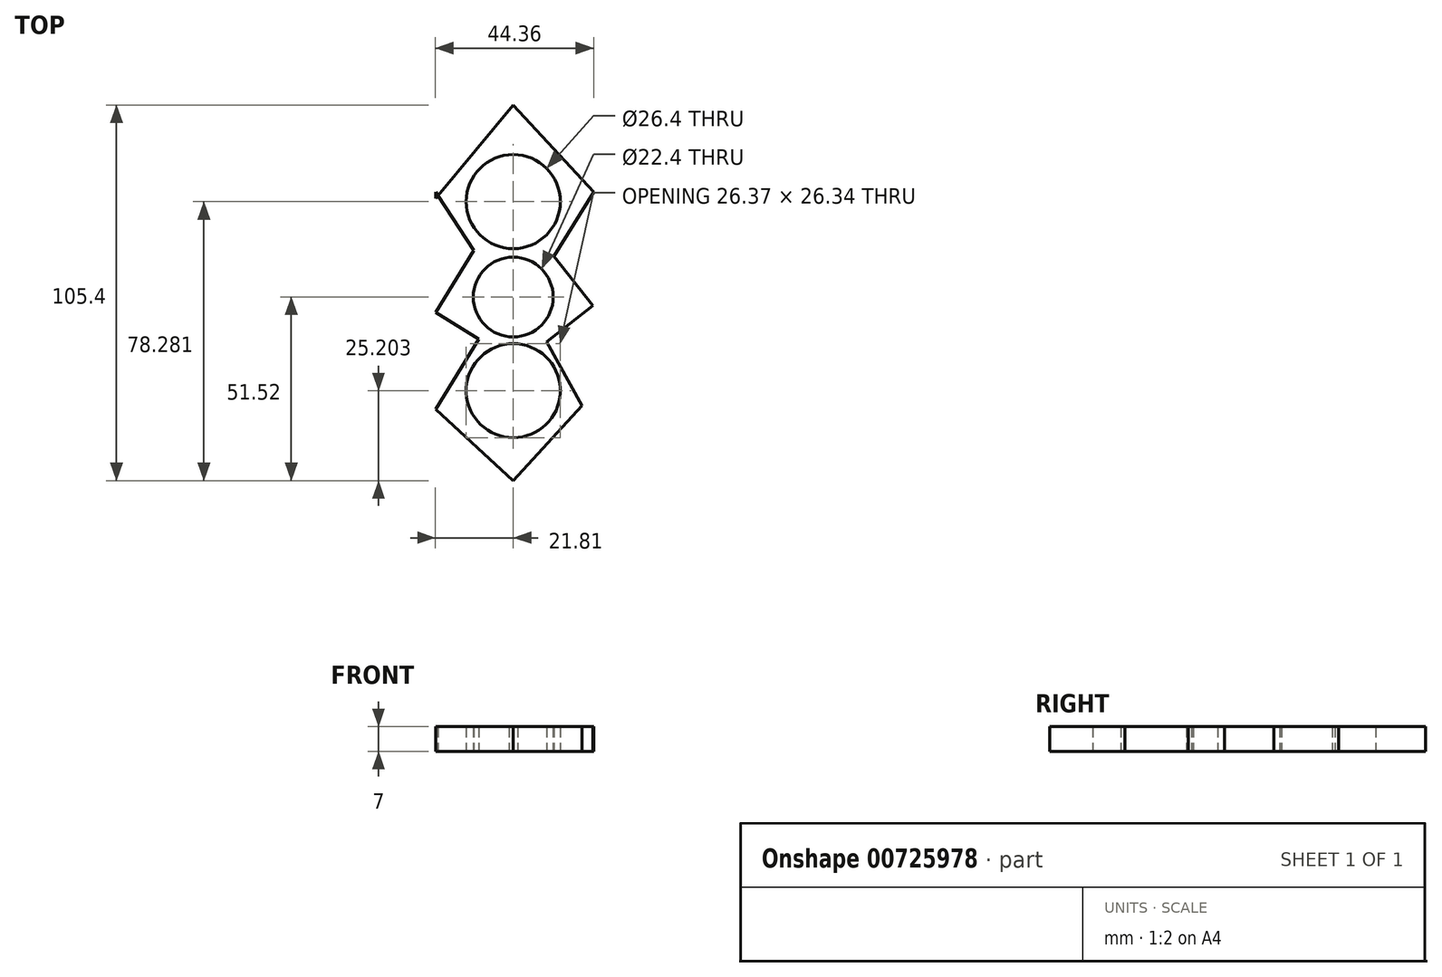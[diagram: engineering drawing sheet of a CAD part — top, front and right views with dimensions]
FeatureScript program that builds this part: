
annotation { "Feature Type Name" : "Feature", "Feature Type Description" : "" }
export const myFeature = defineFeature(function(context is Context, id is Id, definition is map)
    precondition{}
    {
        {
            var Q0;
            Q0=qCreatedBy(makeId("Top.planeOp"),FACE);
            var sketch = newSketch(context, id + "F0", { "sketchPlane" : qUnion([Q0])});
            skCircle(sketch, "E0", {"center": v(0, 26.76) * mm, "radius": 13.2 * mm});
            skCircle(sketch, "E1", {"center": v(0, 26.76) * mm, "radius": 11.2 * mm});
            skCircle(sketch, "E2", {"center": v(0, 0) * mm, "radius": 11.2 * mm});
            skArc(sketch, "E3", {"start": v(-1.2, -13.14) * mm, "mid": v(0, -39.49) * mm, "end": v(1.2, -13.14) * mm});
            skCircle(sketch, "E4", {"center": v(0, -26.29) * mm, "radius": 11.2 * mm});
            skLineSegment(sketch, "E5", {"start": v(-1.2, -13.14) * mm, "end": v(1.2, -13.14) * mm});
            skLineSegment(sketch, "E6", {"start": v(-21.8, 29.5) * mm, "end": v(-21.8, 27.7) * mm});
            skLineSegment(sketch, "E7", {"start": v(-21.8, 29.5) * mm, "end": v(-11.1, 13.07) * mm});
            skLineSegment(sketch, "E8", {"start": v(-11.1, 13.07) * mm, "end": v(-21.8, -4.36) * mm});
            skLineSegment(sketch, "E9", {"start": v(-21.8, -4.36) * mm, "end": v(-9.7, -11.8) * mm});
            skLineSegment(sketch, "E10", {"start": v(-9.7, -11.8) * mm, "end": v(-21.8, -31.5) * mm});
            skLineSegment(sketch, "E11", {"start": v(-21.8, -31.5) * mm, "end": v(0, -51.52) * mm});
            skLineSegment(sketch, "E12", {"start": v(0, -51.52) * mm, "end": v(19.31, -30.47) * mm});
            skLineSegment(sketch, "E13", {"start": v(19.31, -30.47) * mm, "end": v(9.31, -12.61) * mm});
            skLineSegment(sketch, "E14", {"start": v(9.31, -12.61) * mm, "end": v(22.28, -2.48) * mm});
            skLineSegment(sketch, "E15", {"start": v(22.28, -2.48) * mm, "end": v(11.43, 11.4) * mm});
            skLineSegment(sketch, "E16", {"start": v(11.43, 11.4) * mm, "end": v(22.55, 29.5) * mm});
            skLineSegment(sketch, "E17", {"start": v(22.55, 29.5) * mm, "end": v(0, 53.88) * mm});
            skLineSegment(sketch, "E18", {"start": v(0, 53.88) * mm, "end": v(-21.8, 27.7) * mm});
            skSolve(sketch);
        }
        {
            var Q0;
            Q0 = qSketchRegion(id + "F0", true);
            extrude(context, id + "F1", {"entities" : qUnion([Q0]), "depth" : 7 * mm, "offsetDistance" : 25 * mm});
        }
    });
